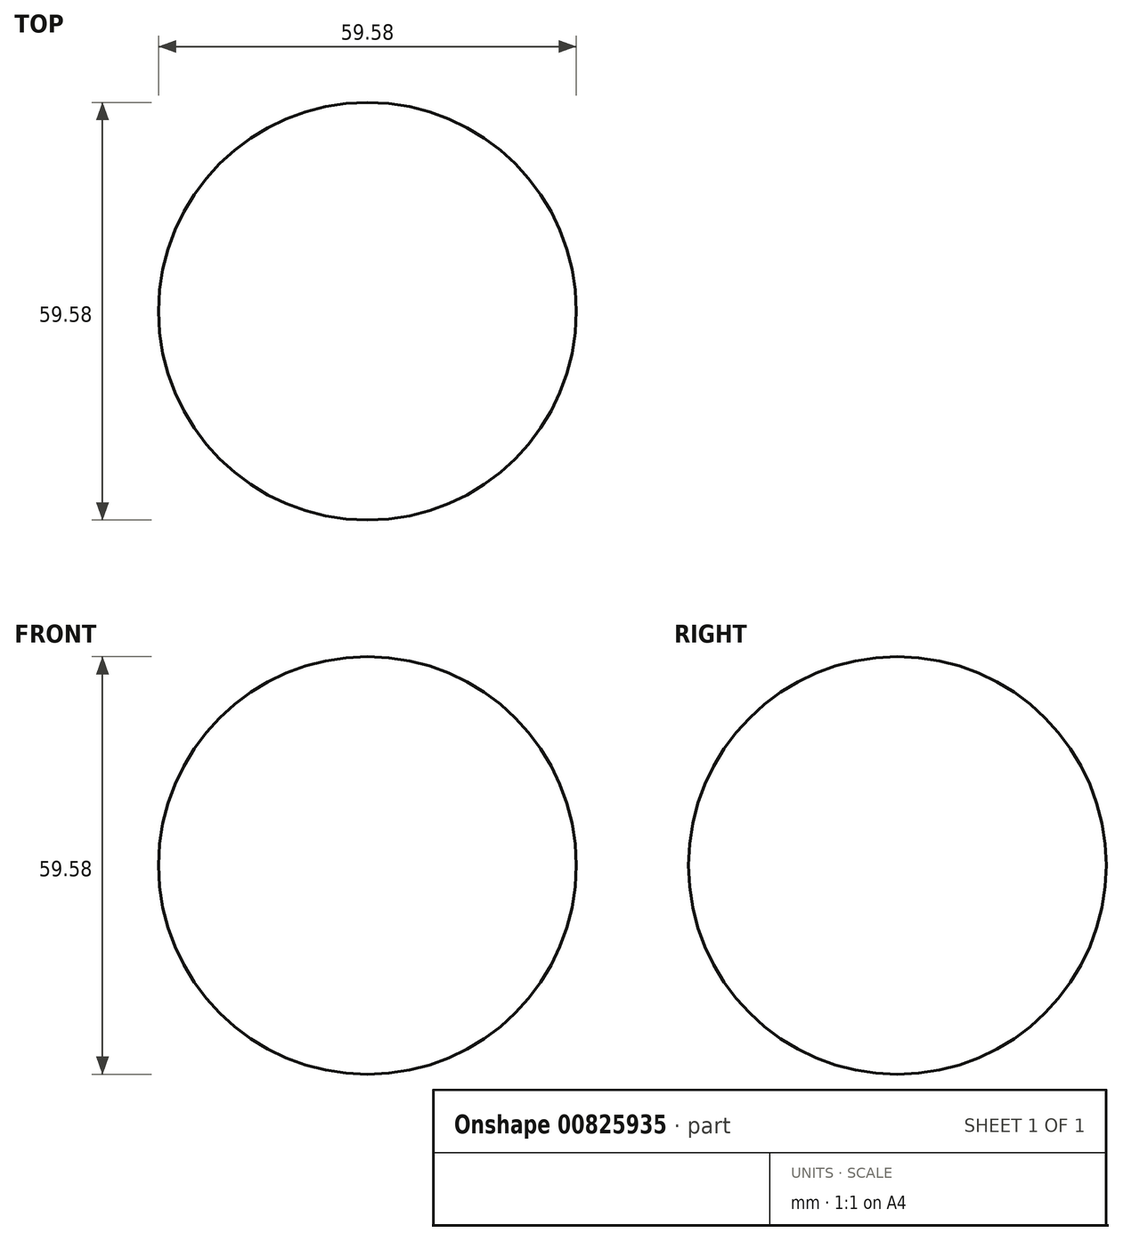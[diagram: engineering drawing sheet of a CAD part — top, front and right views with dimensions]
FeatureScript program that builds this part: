
annotation { "Feature Type Name" : "Feature", "Feature Type Description" : "" }
export const myFeature = defineFeature(function(context is Context, id is Id, definition is map)
    precondition{}
    {
        {
            var Q0;
            Q0=qCreatedBy(makeId("Front.planeOp"),FACE);
            var sketch = newSketch(context, id + "F0", { "sketchPlane" : qUnion([Q0])});
            skCircle(sketch, "E0", {"center": v(0, 0) * mm, "radius": 29.8 * mm});
            skLineSegment(sketch, "E1", {"start": v(0, 29.8) * mm, "end": v(0, -29.8) * mm});
            skSolve(sketch);
        }
        {
            var Q0;
            {var subQ0=sQuery(id+"F0.wireOp",EDGE,"E1");Q0=makeQuery(id+"F0.imprint","IMPRINT",FACE,{"disambiguationData":[TD([[makeQuery(id+"F0.imprint","IMPRINT",EDGE,{"derivedFrom":subQ0}),1.0]])]});}
            var Q1;
            Q1=sQuery(id+"F0.wireOp",EDGE,"E1");
            revolve(context, id + "F1", {"surfaceOperationType" : NewSurfaceOperationType.NEW, "entities" : qUnion([Q0]), "axis" : qUnion([Q1]), "revolveType" : RevolveType.FULL});
        }
    });
